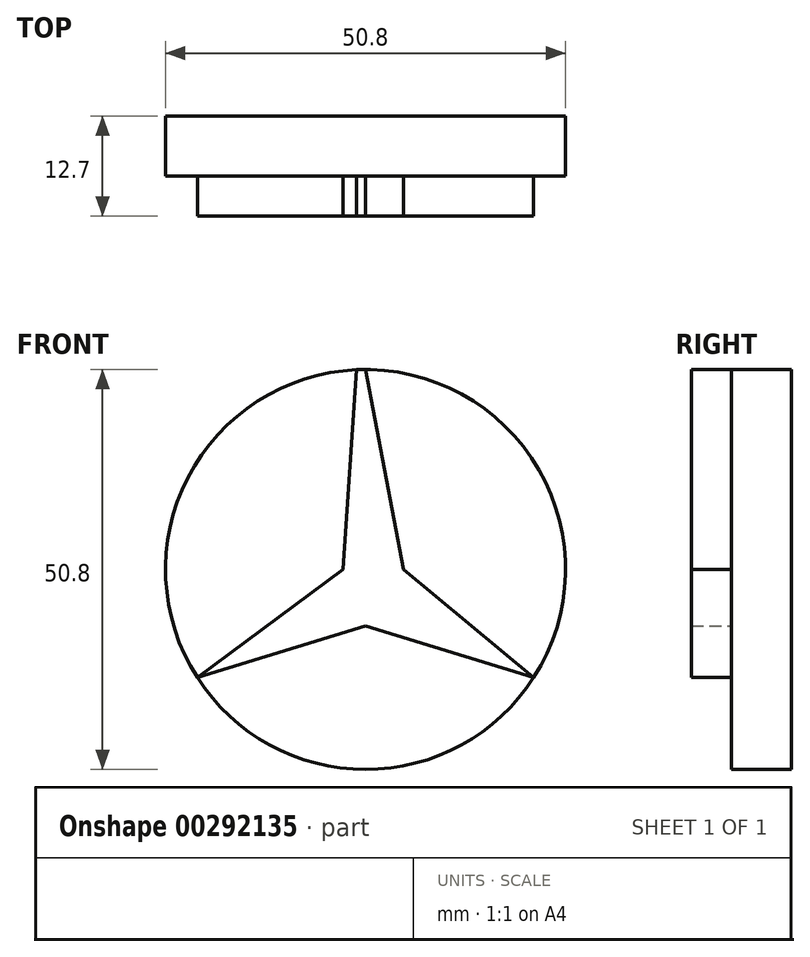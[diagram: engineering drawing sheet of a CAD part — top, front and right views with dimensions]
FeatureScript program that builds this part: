
annotation { "Feature Type Name" : "Feature", "Feature Type Description" : "" }
export const myFeature = defineFeature(function(context is Context, id is Id, definition is map)
    precondition{}
    {
        {
            var Q0;
            Q0=qCreatedBy(makeId("Front.planeOp"),FACE);
            var sketch = newSketch(context, id + "F0", { "sketchPlane" : qUnion([Q0])});
            skCircle(sketch, "E0", {"center": v(0, 0) * mm, "radius": 25.4 * mm});
            skLineSegment(sketch, "E1", {"start": v(-1.15, 25.37) * mm, "end": v(-2.86, 0) * mm});
            skLineSegment(sketch, "E2", {"start": v(-2.86, 0) * mm, "end": v(-21.36, -13.74) * mm});
            skLineSegment(sketch, "E3", {"start": v(-21.36, -13.74) * mm, "end": v(0, -7.2) * mm});
            skLineSegment(sketch, "E4", {"start": v(0, -7.2) * mm, "end": v(21.36, -13.74) * mm});
            skLineSegment(sketch, "E5", {"start": v(21.36, -13.74) * mm, "end": v(4.83, 0) * mm});
            skLineSegment(sketch, "E6", {"start": v(4.83, 0) * mm, "end": v(0, 25.37) * mm});
            skLineSegment(sketch, "E7", {"start": v(-1.15, 25.37) * mm, "end": v(0, 25.37) * mm});
            skSolve(sketch);
        }
        {
            var Q0;
            Q0=makeQuery(id+"F0.imprint","IMPRINT",FACE,{"disambiguationData":[TD([[makeQuery(id+"F0.imprint","IMPRINT",EDGE,{"derivedFrom":sQuery(id+"F0.wireOp",EDGE,"E1")}),1.0]])]});
            extrude(context, id + "F1", {"entities" : qUnion([Q0]), "depth" : 12.7 * mm});
        }
        {
            var Q0;
            Q0=qCreatedBy(makeId("Front.planeOp"),FACE);
            var sketch = newSketch(context, id + "F2", { "sketchPlane" : qUnion([Q0])});
            skCircle(sketch, "E8", {"center": v(0, 0) * mm, "radius": 25.4 * mm});
            skSolve(sketch);
        }
        {
            var Q0;
            Q0=makeQuery(id+"F2.imprint","IMPRINT",FACE,{"disambiguationData":[TD([[makeQuery(id+"F2.imprint","IMPRINT",EDGE,{"derivedFrom":sQuery(id+"F2.wireOp",EDGE,"E8")}),1.0]])]});
            extrude(context, id + "F3", {"entities" : qUnion([Q0]), "operationType" : NewBodyOperationType.ADD, "depth" : 7.62 * mm});
        }
    });
